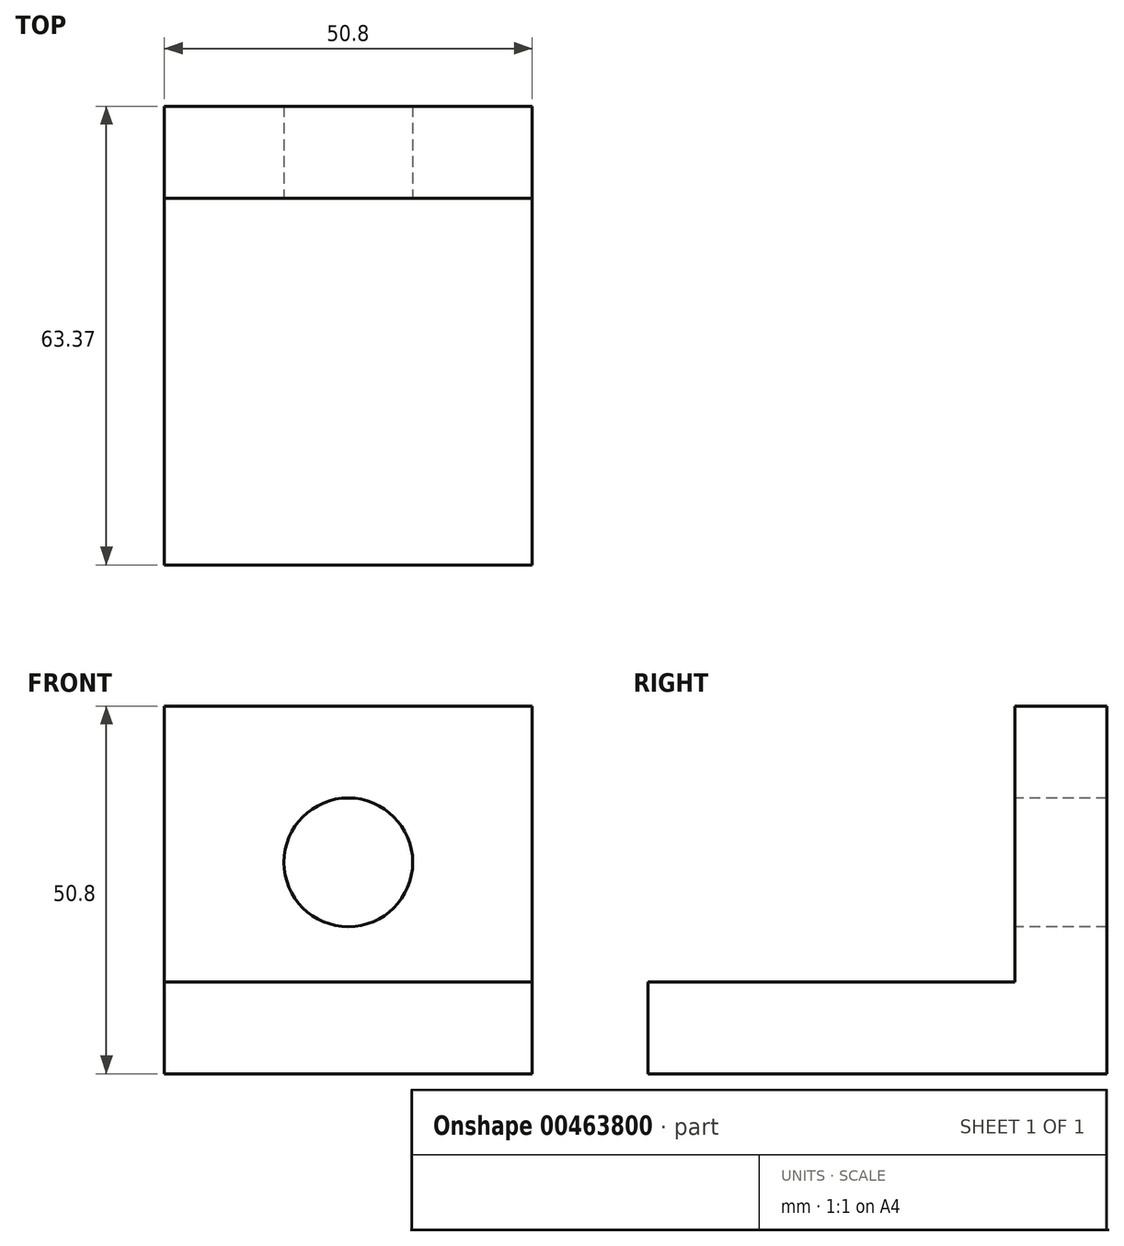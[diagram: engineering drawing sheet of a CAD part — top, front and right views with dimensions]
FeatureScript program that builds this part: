
annotation { "Feature Type Name" : "Feature", "Feature Type Description" : "" }
export const myFeature = defineFeature(function(context is Context, id is Id, definition is map)
    precondition{}
    {
        {
            var Q0;
            Q0=qCreatedBy(makeId("Top.planeOp"),FACE);
            var sketch = newSketch(context, id + "F0", { "sketchPlane" : qUnion([Q0])});
            skLineSegment(sketch, "E0.bottom", {"start": v(25.4, -25.4) * mm, "end": v(-25.4, -25.4) * mm});
            skLineSegment(sketch, "E0.top", {"start": v(25.4, 25.4) * mm, "end": v(-25.4, 25.4) * mm});
            skLineSegment(sketch, "E0.left", {"start": v(25.4, -25.4) * mm, "end": v(25.4, 25.4) * mm});
            skLineSegment(sketch, "E0.right", {"start": v(-25.4, -25.4) * mm, "end": v(-25.4, 25.4) * mm});
            skPoint(sketch, "E0.middle", {"position": v(0, 0) * mm});
            skSolve(sketch);
        }
        {
            var Q0;
            Q0=makeQuery(id+"F0.imprint","IMPRINT",FACE,{"disambiguationData":[TD([[makeQuery(id+"F0.imprint","IMPRINT",EDGE,{"derivedFrom":sQuery(id+"F0.wireOp",EDGE,"E0.bottom")}),-1.0]])]});
            extrude(context, id + "F1", {"entities" : qUnion([Q0]), "depth" : 12.7 * mm});
        }
        {
            var Q0;
            Q0=qCreatedBy(makeId("Top.planeOp"),FACE);
            var sketch = newSketch(context, id + "F2", { "sketchPlane" : qUnion([Q0])});
            skLineSegment(sketch, "E1.bottom", {"start": v(25.4, 37.97) * mm, "end": v(-25.4, 37.97) * mm});
            skLineSegment(sketch, "E1.top", {"start": v(25.4, 25.27) * mm, "end": v(-25.4, 25.27) * mm});
            skLineSegment(sketch, "E1.left", {"start": v(25.4, 37.97) * mm, "end": v(25.4, 25.27) * mm});
            skLineSegment(sketch, "E1.right", {"start": v(-25.4, 37.97) * mm, "end": v(-25.4, 25.27) * mm});
            skPoint(sketch, "E1.middle", {"position": v(0, 31.62) * mm});
            skSolve(sketch);
        }
        {
            var Q0;
            Q0=makeQuery(id+"F2.imprint","IMPRINT",FACE,{"disambiguationData":[TD([[makeQuery(id+"F2.imprint","IMPRINT",EDGE,{"derivedFrom":sQuery(id+"F2.wireOp",EDGE,"E1.bottom")}),1.0]])]});
            extrude(context, id + "F3", {"entities" : qUnion([Q0]), "operationType" : NewBodyOperationType.ADD, "depth" : 50.8 * mm});
        }
        {
            var Q0;
            Q0=makeQuery(id+"F3.opExtrude","SWEPT_FACE",FACE,{"disambiguationData":[OSD([sQuery(id+"F2.wireOp",EDGE,"E1.top")])]});
            var sketch = newSketch(context, id + "F4", { "sketchPlane" : qUnion([Q0])});
            skCircle(sketch, "E2", {"center": v(0, 29.21) * mm, "radius": 8.9 * mm});
            skLineSegment(sketch, "E3", {"start": v(0, 38.1) * mm, "end": v(0, 50.8) * mm});
            skSolve(sketch);
        }
        {
            var Q0;
            Q0=makeQuery(id+"F4.imprint","IMPRINT",FACE,{"disambiguationData":[TD([[makeQuery(id+"F4.imprint","IMPRINT",EDGE,{"derivedFrom":sQuery(id+"F4.wireOp",EDGE,"E2")}),1.0]])]});
            extrude(context, id + "F5", {"entities" : qUnion([Q0]), "operationType" : NewBodyOperationType.REMOVE, "oppositeDirection" : true, "depth" : 12.7 * mm});
        }
    });
